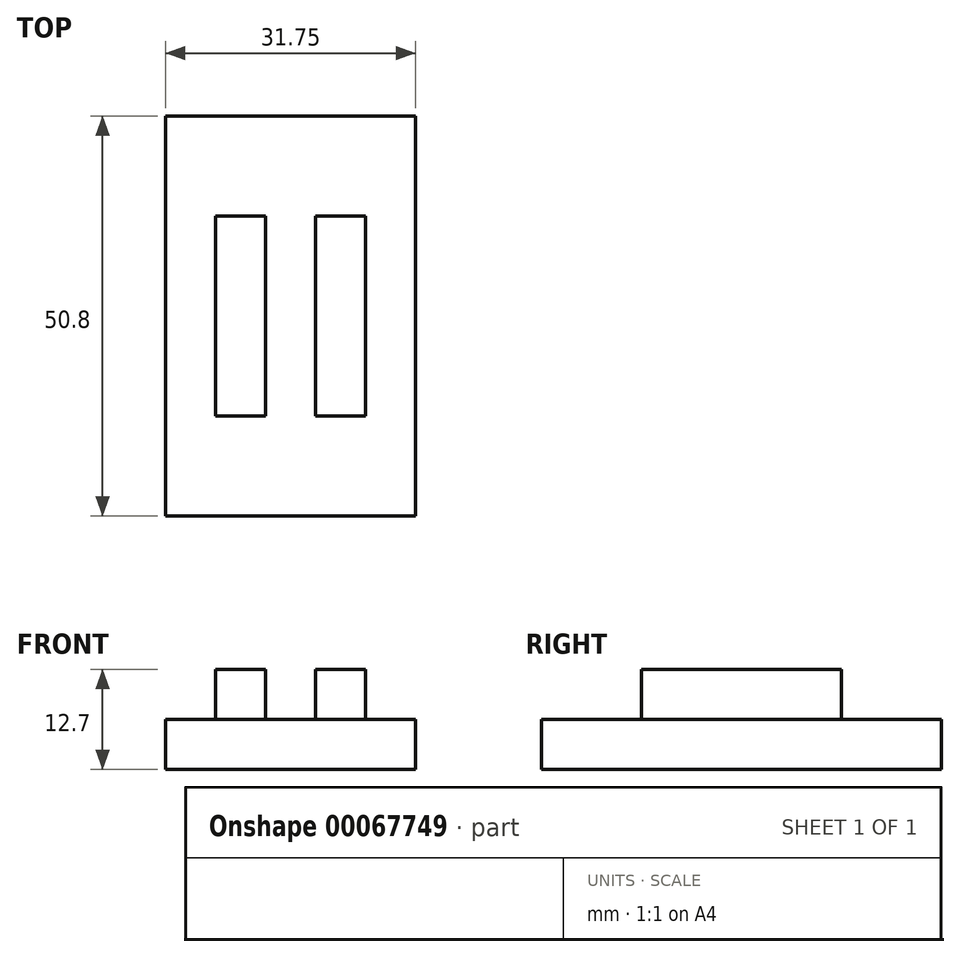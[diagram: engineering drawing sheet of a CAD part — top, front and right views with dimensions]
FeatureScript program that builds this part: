
annotation { "Feature Type Name" : "Feature", "Feature Type Description" : "" }
export const myFeature = defineFeature(function(context is Context, id is Id, definition is map)
    precondition{}
    {
        {
            var Q0;
            Q0=qCreatedBy(makeId("Top.planeOp"),FACE);
            var sketch = newSketch(context, id + "F0", { "sketchPlane" : qUnion([Q0])});
            skLineSegment(sketch, "E0.bottom", {"start": v(-157.4, -106.9) * mm, "end": v(-125.66, -106.9) * mm});
            skLineSegment(sketch, "E0.top", {"start": v(-157.4, -56.1) * mm, "end": v(-125.66, -56.1) * mm});
            skLineSegment(sketch, "E0.left", {"start": v(-157.4, -106.9) * mm, "end": v(-157.4, -56.1) * mm});
            skLineSegment(sketch, "E0.right", {"start": v(-125.66, -106.9) * mm, "end": v(-125.66, -56.1) * mm});
            skSolve(sketch);
        }
        {
            var Q0;
            Q0 = qSketchRegion(id + "F0", true);
            extrude(context, id + "F1", {"entities" : qUnion([Q0]), "depth" : 6.35 * mm});
        }
        {
            var Q0;
            Q0=makeQuery(id+"F1.opExtrude","CAP_FACE",FACE,{"disambiguationData":[OSD([sQuery(id+"F0.wireOp",EDGE,"E0.bottom"),sQuery(id+"F0.wireOp",EDGE,"E0.top"),sQuery(id+"F0.wireOp",EDGE,"E0.left"),sQuery(id+"F0.wireOp",EDGE,"E0.right")])],"isStart":false});
            var sketch = newSketch(context, id + "F2", { "sketchPlane" : qUnion([Q0])});
            skLineSegment(sketch, "E1.bottom", {"start": v(-151.06, -68.8) * mm, "end": v(-144.7, -68.8) * mm});
            skLineSegment(sketch, "E1.top", {"start": v(-151.06, -94.2) * mm, "end": v(-144.7, -94.2) * mm});
            skLineSegment(sketch, "E1.left", {"start": v(-151.06, -68.8) * mm, "end": v(-151.06, -94.2) * mm});
            skLineSegment(sketch, "E1.right", {"start": v(-144.7, -68.8) * mm, "end": v(-144.7, -94.2) * mm});
            skLineSegment(sketch, "E2.1.0.0", {"start": v(-138.36, -68.8) * mm, "end": v(-132, -68.8) * mm});
            skLineSegment(sketch, "E2.1.0.1", {"start": v(-138.36, -94.2) * mm, "end": v(-132, -94.2) * mm});
            skLineSegment(sketch, "E2.1.0.2", {"start": v(-138.36, -68.8) * mm, "end": v(-138.36, -94.2) * mm});
            skLineSegment(sketch, "E2.1.0.3", {"start": v(-132, -68.8) * mm, "end": v(-132, -94.2) * mm});
            skLineSegment(sketch, "E2.direction1", {"start": v(-151.06, -68.8) * mm, "end": v(-138.36, -68.8) * mm, "construction": true});
            skSolve(sketch);
        }
        {
            var Q0;
            Q0 = qSketchRegion(id + "F2", true);
            extrude(context, id + "F3", {"entities" : qUnion([Q0]), "operationType" : NewBodyOperationType.ADD, "depth" : 6.35 * mm});
        }
    });
